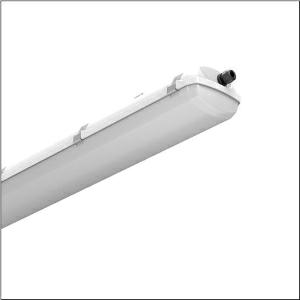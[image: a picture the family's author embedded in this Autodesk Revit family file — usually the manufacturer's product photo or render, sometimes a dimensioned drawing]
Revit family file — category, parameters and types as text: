
# Revit family: monsun_r__ex_51fxb27l440a_d684
name_source: partatom
category: Lighting Fixtures
units: mm (PartAtom-declared; Revit-internal decimal feet)

## family parameters
Cut with Voids When Loaded = No
Host = Face
Light Source = No
Part Type = Normal
Room Calculation Point = No
Round Connector Dimension = Use Diameter
Shared = No

## types (1)
- Monsun® Ex (1 x LED, 4500 lm, 29.2 W, 4000K)
    Apparent Load = 29 VA
    CIE Flux Codes = 43 73 91 93 100
    Color Rendering = 80
    Color Temperature = 4000K
    Default Elevation = 1800 mm
    Description = Monsun® Ex, damp-proof luminaire, primary optical cover: cover, of PC, UV-stabilised, opal, light emission: direct distribution, primary light characteristic: symmetric, installation type: surface-mounted, LED, rated luminous flux: 4.500lm, luminous efficacy: 154lm/W, light colour: 840, colour temperature: 4000K, control gear: ECG, with terminal, 3-pole, max. 2.5mm², through-wiring: 5x 2.5mm², mains connection: 220..240V, AC, 50/60Hz, rated input power: 29W, housing, of PC, light grey (RAL 7035), incl. blind plug, incl. 1x Ex cable gland M20 for cable diameter 7..12mm with sealing, length: 1.280mm, width: 155mm, height: 105mm, clip for enclosure, of stainless steel, protection rating (complete): IP66, insulation class (complete): insulation class I (protective earthing), certification: CE, explosion class: zone2,22 II 3G Ex nR IIC T6 GC, II 3D Ex tc IIIC T80°C Dc, impact resistance: IK10, permissible operating ambient temperature: -20..+60°C, LABS conformity tested according to VDMA 24364:2018-05, contact your sales advisor before using the luminaires in applications with unclear chemical exposure, large temperature fluctuations or condensation-forming humidity, packaging unit: 1 piece
    Height = 105 mm
    Lamp = 1 x LED
    Lamp Light Flux = 4500 lm
    Lamp Power = 29.2 W
    Lamp count = 1
    Length = 1280 mm
    Luminous efficacy = 154 lm/W
    Manufacturer = Siteco
    ModVariant = No
    Model = 51FXB27L440A
    Mounting Place = Ceiling
    Mounting Type = Surface mounted
    Number of Poles = 1
    OnlyDefault = Yes
    Power Factor = 1
    Product Name = Monsun® Ex
    Product group = damp-proof luminaire
    ProductGroupID = 300
    Protection Class = Protection class I
    Protection Degree = IP 66
    RLX_Detail_Level = 1
    RLX_Emergency_Light_Flux = 0 lm
    RLX_Emergency_Type = 0
    RLX_Emergency_Type_DB = No
    RlxData = <blob elided: 41665 chars, md5=dace1659>
    Socket = socket
    Standby Power = 0 W
    System Light Flux = 4500 lm
    System Power = 29 W
    Type Comments = Product without accessories
    Type Image = l_1258882.jpg
    URL = http://relux.com
    VarID = ---
    Voltage = 0 V
    Weight = 0.00 kg
    Width = 155 mm

## geometry (parser evidence)
native form markers: Blend x4, Sweep x12
no freeform markers — native parametric forms only
